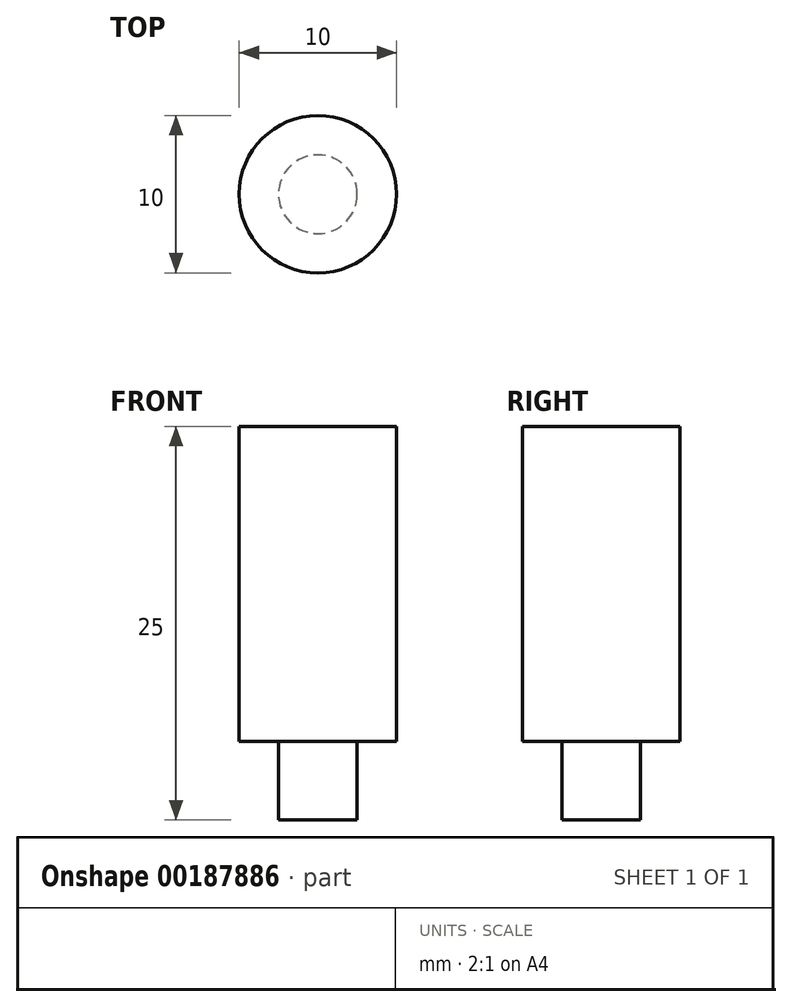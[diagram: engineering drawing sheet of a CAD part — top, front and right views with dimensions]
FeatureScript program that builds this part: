
annotation { "Feature Type Name" : "Feature", "Feature Type Description" : "" }
export const myFeature = defineFeature(function(context is Context, id is Id, definition is map)
    precondition{}
    {
        {
            var Q0;
            Q0=qCreatedBy(makeId("Front.planeOp"),FACE);
            var sketch = newSketch(context, id + "F0", { "sketchPlane" : qUnion([Q0])});
            skLineSegment(sketch, "E0.bottom", {"start": v(0, 0) * mm, "end": v(-2.5, 0) * mm});
            skLineSegment(sketch, "E0.top", {"start": v(0, 5) * mm, "end": v(-2.5, 5) * mm});
            skLineSegment(sketch, "E0.left", {"start": v(0, 0) * mm, "end": v(0, 5) * mm});
            skLineSegment(sketch, "E0.right", {"start": v(-2.5, 0) * mm, "end": v(-2.5, 5) * mm});
            skLineSegment(sketch, "E1.bottom", {"start": v(0, 5) * mm, "end": v(-5, 5) * mm});
            skLineSegment(sketch, "E1.top", {"start": v(0, 25) * mm, "end": v(-5, 25) * mm});
            skLineSegment(sketch, "E1.left", {"start": v(0, 5) * mm, "end": v(0, 25) * mm});
            skLineSegment(sketch, "E1.right", {"start": v(-5, 5) * mm, "end": v(-5, 25) * mm});
            skSolve(sketch);
        }
        {
            var Q0;
            Q0=makeQuery(id+"F0.imprint","IMPRINT",FACE,{"disambiguationData":[TD([[makeQuery(id+"F0.imprint","IMPRINT",EDGE,{"derivedFrom":sQuery(id+"F0.wireOp",EDGE,"E1.top")}),1.0]])]});
            var Q1;
            Q1=makeQuery(id+"F0.imprint","IMPRINT",FACE,{"disambiguationData":[TD([[makeQuery(id+"F0.imprint","IMPRINT",EDGE,{"derivedFrom":sQuery(id+"F0.wireOp",EDGE,"E0.bottom")}),-1.0]])]});
            var Q2;
            Q2=sQuery(id+"F0.wireOp",EDGE,"E1.left");
            revolve(context, id + "F1", {"entities" : qUnion([Q0, Q1]), "axis" : qUnion([Q2]), "revolveType" : RevolveType.FULL});
        }
    });
